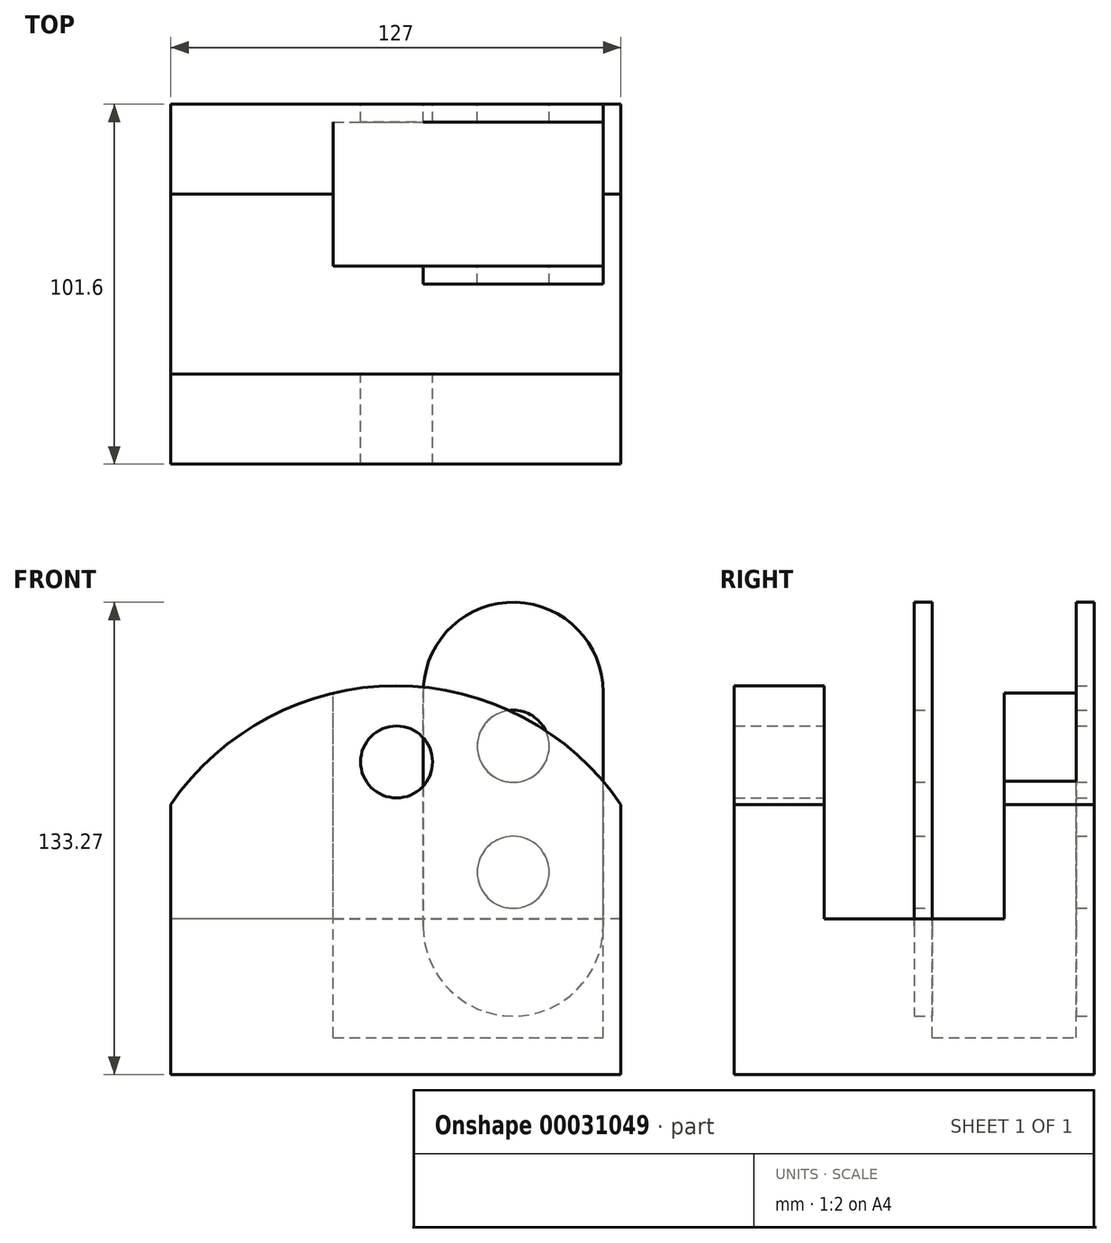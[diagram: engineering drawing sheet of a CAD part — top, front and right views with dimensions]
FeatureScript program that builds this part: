
annotation { "Feature Type Name" : "Feature", "Feature Type Description" : "" }
export const myFeature = defineFeature(function(context is Context, id is Id, definition is map)
    precondition{}
    {
        {
            var Q0;
            Q0=qCreatedBy(makeId("Front.planeOp"),FACE);
            var sketch = newSketch(context, id + "F0", { "sketchPlane" : qUnion([Q0])});
            skLineSegment(sketch, "E0.top", {"start": v(-63.68, -49.8) * mm, "end": v(63.32, -49.8) * mm});
            skLineSegment(sketch, "E0.left", {"start": v(-63.68, 26.4) * mm, "end": v(-63.68, -49.8) * mm});
            skLineSegment(sketch, "E0.right", {"start": v(63.32, 26.4) * mm, "end": v(63.32, -49.8) * mm});
            skArc(sketch, "E1", {"start": v(63.32, 26.4) * mm, "mid": v(-0.18, 59.89) * mm, "end": v(-63.68, 26.4) * mm});
            skCircle(sketch, "E2", {"center": v(0, 38.4) * mm, "radius": 10.16 * mm});
            skSolve(sketch);
        }
        {
            var Q0;
            Q0=makeQuery(id+"F0.imprint","IMPRINT",FACE,{"disambiguationData":[TD([[makeQuery(id+"F0.imprint","IMPRINT",EDGE,{"derivedFrom":sQuery(id+"F0.wireOp",EDGE,"E0.top")}),1.0]])]});
            extrude(context, id + "F1", {"entities" : qUnion([Q0]), "depth" : 101.6 * mm});
        }
        {
            var Q0;
            Q0=makeQuery(id+"F1.opExtrude","SWEPT_FACE",FACE,{"disambiguationData":[OSD([sQuery(id+"F0.wireOp",EDGE,"E0.left")])]});
            var sketch = newSketch(context, id + "F2", { "sketchPlane" : qUnion([Q0])});
            skLineSegment(sketch, "E3.bottom", {"start": v(25.4, -5.96) * mm, "end": v(76.2, -5.96) * mm});
            skLineSegment(sketch, "E3.top", {"start": v(25.4, 70.85) * mm, "end": v(76.2, 70.85) * mm});
            skLineSegment(sketch, "E3.left", {"start": v(25.4, -5.96) * mm, "end": v(25.4, 70.85) * mm});
            skLineSegment(sketch, "E3.right", {"start": v(76.2, -5.96) * mm, "end": v(76.2, 70.85) * mm});
            skPoint(sketch, "E4.end.orphan", {"position": v(76.2, -5.96) * mm});
            skPoint(sketch, "E4.start.orphan", {"position": v(101.6, -5.96) * mm});
            skSolve(sketch);
        }
        {
            var Q0;
            {var subQ5=sQuery(id+"F2.wireOp",EDGE,"E3.bottom");Q0=makeQuery(id+"F2.imprint","IMPRINT",FACE,{"disambiguationData":[TD([[makeQuery(id+"F2.imprint","IMPRINT",EDGE,{"derivedFrom":subQ5}),1.0]])]});}
            var Q1;
            {var subQ5=sQuery(id+"F2.wireOp",EDGE,"E3.top");Q1=makeQuery(id+"F2.imprint","IMPRINT",FACE,{"disambiguationData":[TD([[makeQuery(id+"F2.imprint","IMPRINT",EDGE,{"derivedFrom":subQ5}),-1.0]])]});}
            extrude(context, id + "F3", {"entities" : qUnion([Q0, Q1]), "operationType" : NewBodyOperationType.REMOVE, "oppositeDirection" : true, "depth" : 254 * mm});
        }
        {
            var Q0;
            Q0=qCreatedBy(makeId("Front.planeOp"),FACE);
            var sketch = newSketch(context, id + "F4", { "sketchPlane" : qUnion([Q0])});
            skCircle(sketch, "E5", {"center": v(32.92, 42.83) * mm, "radius": 10.16 * mm});
            skLineSegment(sketch, "E6.left", {"start": v(7.52, 42.83) * mm, "end": v(7.52, -7.97) * mm});
            skLineSegment(sketch, "E6.right", {"start": v(58.32, 42.83) * mm, "end": v(58.32, -7.97) * mm});
            skLineSegment(sketch, "E7.left", {"start": v(58.32, 42.83) * mm, "end": v(58.32, 58.07) * mm});
            skLineSegment(sketch, "E7.right", {"start": v(7.52, 42.83) * mm, "end": v(7.52, 58.07) * mm});
            skArc(sketch, "E8", {"start": v(58.32, 58.07) * mm, "mid": v(32.92, 83.47) * mm, "end": v(7.52, 58.07) * mm});
            skArc(sketch, "E9", {"start": v(7.52, -7.97) * mm, "mid": v(32.92, -33.37) * mm, "end": v(58.32, -7.97) * mm});
            skLineSegment(sketch, "E10", {"start": v(32.92, 52.99) * mm, "end": v(32.92, 83.47) * mm});
            skCircle(sketch, "E11", {"center": v(32.92, 7.27) * mm, "radius": 10.16 * mm});
            skSolve(sketch);
        }
        {
            var Q0;
            Q0=makeQuery(id+"F4.imprint","IMPRINT",FACE,{"disambiguationData":[TD([[makeQuery(id+"F4.imprint","IMPRINT",EDGE,{"derivedFrom":sQuery(id+"F4.wireOp",EDGE,"E5")}),-1.0]])]});
            extrude(context, id + "F5", {"entities" : qUnion([Q0]), "depth" : 50.8 * mm});
        }
        {
            var Q0;
            Q0=makeQuery(id+"F5.opExtrude","SWEPT_FACE",FACE,{"disambiguationData":[OSD([sQuery(id+"F4.wireOp",EDGE,"E6.right"),sQuery(id+"F4.wireOp",EDGE,"E7.left")])]});
            var sketch = newSketch(context, id + "F6", { "sketchPlane" : qUnion([Q0])});
            skPoint(sketch, "E12.end.orphan", {"position": v(0, -33.96) * mm});
            skLineSegment(sketch, "E13", {"start": v(-50.8, -7.97) * mm, "end": v(-45.72, -7.97) * mm});
            skLineSegment(sketch, "E14", {"start": v(0, -7.97) * mm, "end": v(-5.08, -7.97) * mm});
            skLineSegment(sketch, "E15.bottom", {"start": v(-45.72, -39.4) * mm, "end": v(-5.08, -39.4) * mm});
            skLineSegment(sketch, "E15.top", {"start": v(-45.72, 92.18) * mm, "end": v(-5.08, 92.18) * mm});
            skLineSegment(sketch, "E15.left", {"start": v(-45.72, -39.4) * mm, "end": v(-45.72, 92.18) * mm});
            skLineSegment(sketch, "E15.right", {"start": v(-5.08, -39.4) * mm, "end": v(-5.08, 92.18) * mm});
            skSolve(sketch);
        }
        {
            var Q0;
            {var subQ5=sQuery(id+"F6.wireOp",EDGE,"E15.top");Q0=makeQuery(id+"F6.imprint","IMPRINT",FACE,{"disambiguationData":[TD([[makeQuery(id+"F6.imprint","IMPRINT",EDGE,{"derivedFrom":subQ5}),-1.0]])]});}
            var Q1;
            {var subQ0=makeQuery(id+"F5.opExtrude","SWEPT_EDGE",EDGE,{"disambiguationData":[OSD([sQuery(id+"F4.wireOp",EDGE,"E7.left"),sQuery(id+"F4.wireOp",EDGE,"E8")])]});var subQ3=sQuery(id+"F6.wireOp",EDGE,"E15.left");var subQ4=makeQuery(id+"F6.imprint","INTERSECT",VERTEX,{"derivedFrom":[subQ0,subQ3]});Q1=makeQuery(id+"F6.imprint","IMPRINT",FACE,{"disambiguationData":[TD([[makeQuery(id+"F6.imprint","IMPRINT",EDGE,{"disambiguationData":[TD([[subQ4,1.0]])],"derivedFrom":subQ3}),-1.0]])]});}
            var Q2;
            {var subQ5=sQuery(id+"F6.wireOp",EDGE,"E15.bottom");Q2=makeQuery(id+"F6.imprint","IMPRINT",FACE,{"disambiguationData":[TD([[makeQuery(id+"F6.imprint","IMPRINT",EDGE,{"derivedFrom":subQ5}),1.0]])]});}
            extrude(context, id + "F7", {"entities" : qUnion([Q0, Q1, Q2]), "operationType" : NewBodyOperationType.REMOVE, "oppositeDirection" : true, "depth" : 76.2 * mm});
        }
    });
